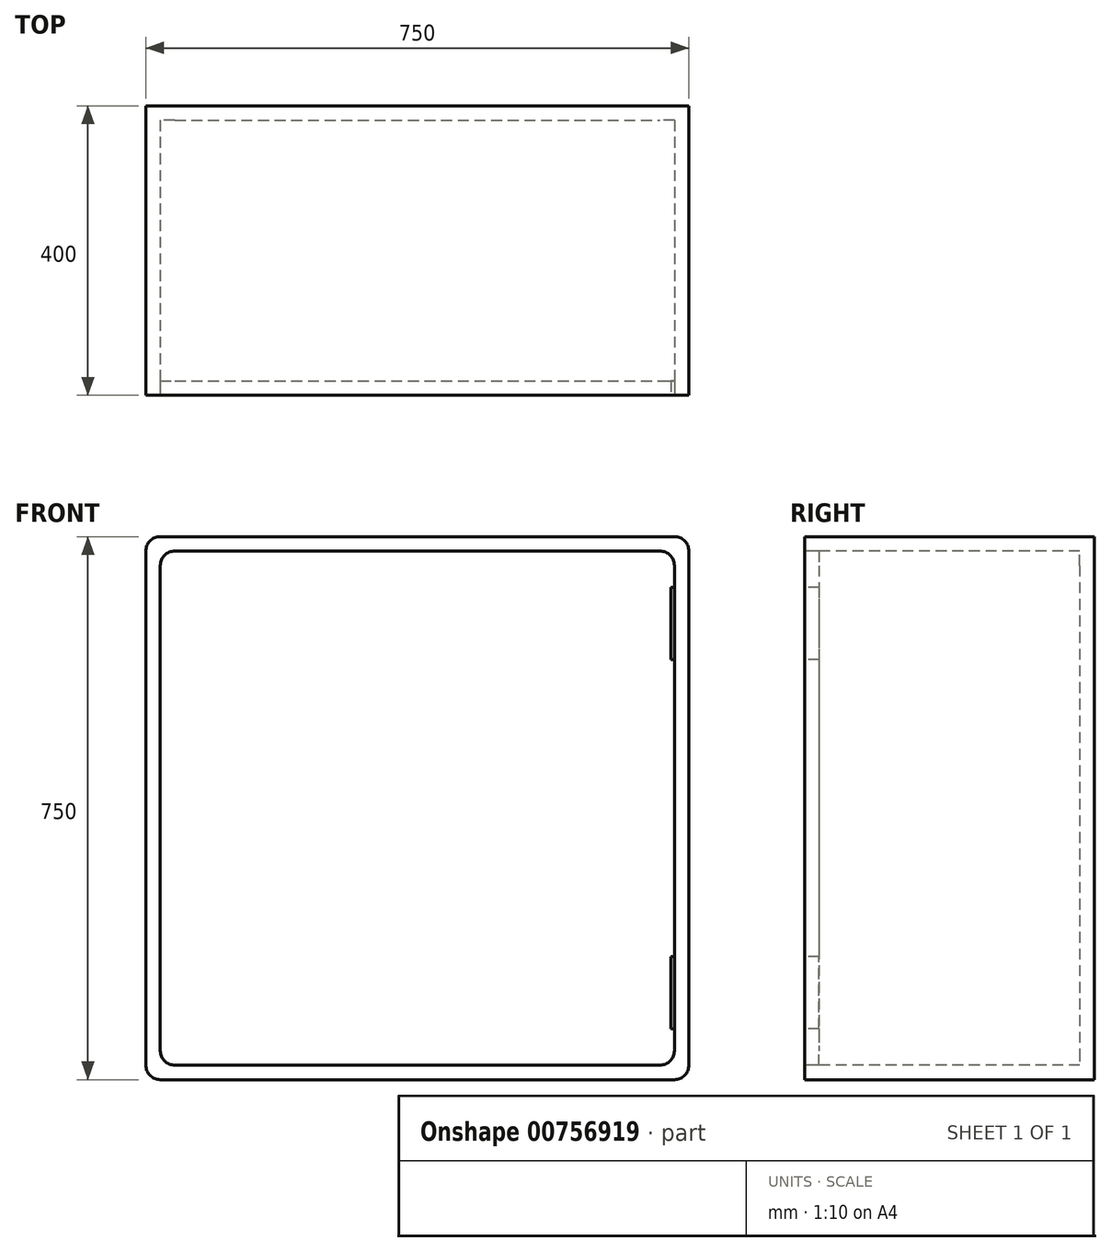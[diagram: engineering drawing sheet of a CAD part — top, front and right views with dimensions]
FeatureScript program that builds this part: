
annotation { "Feature Type Name" : "Feature", "Feature Type Description" : "" }
export const myFeature = defineFeature(function(context is Context, id is Id, definition is map)
    precondition{}
    {
        {
            var Q0;
            Q0=qCreatedBy(makeId("Front.planeOp"),FACE);
            var sketch = newSketch(context, id + "F0", { "sketchPlane" : qUnion([Q0])});
            skLineSegment(sketch, "E0.bottom", {"start": v(0, -20) * mm, "end": v(710, -20) * mm});
            skLineSegment(sketch, "E0.top", {"start": v(0, 730) * mm, "end": v(710, 730) * mm});
            skLineSegment(sketch, "E0.left", {"start": v(-20, 0) * mm, "end": v(-20, 710) * mm});
            skLineSegment(sketch, "E0.right", {"start": v(730, 0) * mm, "end": v(730, 710) * mm});
            skLineSegment(sketch, "E1.bottom", {"start": v(20, 710) * mm, "end": v(690, 710) * mm});
            skLineSegment(sketch, "E1.top", {"start": v(20, 0) * mm, "end": v(690, 0) * mm});
            skLineSegment(sketch, "E1.left", {"start": v(0, 690) * mm, "end": v(0, 20) * mm});
            skLineSegment(sketch, "E1.right", {"start": v(710, 690) * mm, "end": v(710, 20) * mm});
            skPoint(sketch, "E2.visualSharp", {"position": v(0, 710) * mm});
            skArc(sketch, "E2.filletArc", {"start": v(20, 710) * mm, "mid": v(5.86, 704.14) * mm, "end": v(0, 690) * mm});
            skPoint(sketch, "E3.visualSharp", {"position": v(-20, 730) * mm});
            skArc(sketch, "E3.filletArc", {"start": v(0, 730) * mm, "mid": v(-14.14, 724.14) * mm, "end": v(-20, 710) * mm});
            skArc(sketch, "E4.filletArc", {"start": v(730, 710) * mm, "mid": v(724.14, 724.14) * mm, "end": v(710, 730) * mm});
            skArc(sketch, "E5.filletArc", {"start": v(710, 690) * mm, "mid": v(704.14, 704.14) * mm, "end": v(690, 710) * mm});
            skPoint(sketch, "E6.visualSharp", {"position": v(730, -20) * mm});
            skArc(sketch, "E6.filletArc", {"start": v(710, -20) * mm, "mid": v(724.14, -14.14) * mm, "end": v(730, 0) * mm});
            skArc(sketch, "E7.filletArc", {"start": v(690, 0) * mm, "mid": v(704.14, 5.86) * mm, "end": v(710, 20) * mm});
            skPoint(sketch, "E8.visualSharp", {"position": v(-20, -20) * mm});
            skArc(sketch, "E8.filletArc", {"start": v(-20, 0) * mm, "mid": v(-14.14, -14.14) * mm, "end": v(0, -20) * mm});
            skArc(sketch, "E9.filletArc", {"start": v(0, 20) * mm, "mid": v(5.86, 5.86) * mm, "end": v(20, 0) * mm});
            skSolve(sketch);
        }
        {
            var Q0;
            Q0=makeQuery(id+"F0.imprint","IMPRINT",FACE,{"disambiguationData":[TD([[makeQuery(id+"F0.imprint","IMPRINT",EDGE,{"derivedFrom":sQuery(id+"F0.wireOp",EDGE,"E0.bottom")}),1.0]])]});
            var Q1;
            Q1=makeQuery(id+"F0.imprint","IMPRINT",FACE,{"disambiguationData":[TD([[makeQuery(id+"F0.imprint","IMPRINT",EDGE,{"derivedFrom":sQuery(id+"F0.wireOp",EDGE,"E1.bottom")}),-1.0]])]});
            extrude(context, id + "F1", {"entities" : qUnion([Q0, Q1]), "oppositeDirection" : true, "depth" : 400 * mm, "offsetDistance" : 25.4 * mm});
        }
        {
            var Q0;
            Q0=makeQuery(id+"F0.imprint","IMPRINT",FACE,{"disambiguationData":[TD([[makeQuery(id+"F0.imprint","IMPRINT",EDGE,{"derivedFrom":sQuery(id+"F0.wireOp",EDGE,"E1.bottom")}),-1.0]])]});
            extrude(context, id + "F2", {"entities" : qUnion([Q0]), "operationType" : NewBodyOperationType.REMOVE, "oppositeDirection" : true, "depth" : 380 * mm, "offsetDistance" : 25.4 * mm});
        }
        {
            var Q0;
            Q0=makeQuery(id+"F0.imprint","IMPRINT",FACE,{"disambiguationData":[TD([[makeQuery(id+"F0.imprint","IMPRINT",EDGE,{"derivedFrom":sQuery(id+"F0.wireOp",EDGE,"E1.bottom")}),-1.0]])]});
            extrude(context, id + "F3", {"entities" : qUnion([Q0]), "oppositeDirection" : true, "depth" : 20 * mm, "offsetDistance" : 25.4 * mm});
        }
        {
            var Q0;
            Q0=makeQuery(id+"F3.opExtrude","CAP_FACE",FACE,{"disambiguationData":[OSD([sQuery(id+"F0.wireOp",EDGE,"E1.bottom"),sQuery(id+"F0.wireOp",EDGE,"E1.top"),sQuery(id+"F0.wireOp",EDGE,"E1.left"),sQuery(id+"F0.wireOp",EDGE,"E1.right"),sQuery(id+"F0.wireOp",EDGE,"E2.filletArc"),sQuery(id+"F0.wireOp",EDGE,"E5.filletArc"),sQuery(id+"F0.wireOp",EDGE,"E7.filletArc"),sQuery(id+"F0.wireOp",EDGE,"E9.filletArc")])],"isStart":true});
            var sketch = newSketch(context, id + "F4", { "sketchPlane" : qUnion([Q0])});
            skLineSegment(sketch, "E10", {"start": v(710, 660) * mm, "end": v(705, 660) * mm});
            skLineSegment(sketch, "E11", {"start": v(705, 660) * mm, "end": v(705, 560) * mm});
            skLineSegment(sketch, "E12", {"start": v(705, 560) * mm, "end": v(710, 560) * mm});
            skLineSegment(sketch, "E13", {"start": v(710, 50) * mm, "end": v(705, 50) * mm});
            skLineSegment(sketch, "E14", {"start": v(705, 50) * mm, "end": v(705, 150) * mm});
            skLineSegment(sketch, "E15", {"start": v(705, 150) * mm, "end": v(710, 150) * mm});
            skLineSegment(sketch, "E16", {"start": v(710, 150) * mm, "end": v(710, 50) * mm});
            skSolve(sketch);
        }
        {
            var Q0;
            {var subQ0=sQuery(id+"F4.wireOp",EDGE,"E10");Q0=makeQuery(id+"F4.imprint","IMPRINT",FACE,{"disambiguationData":[TD([[makeQuery(id+"F4.imprint","IMPRINT",EDGE,{"derivedFrom":subQ0}),1.0]])]});}
            var Q1;
            Q1=makeQuery(id+"F4.imprint","IMPRINT",FACE,{"disambiguationData":[TD([[makeQuery(id+"F4.imprint","IMPRINT",EDGE,{"derivedFrom":sQuery(id+"F4.wireOp",EDGE,"E13")}),-1.0]])]});
            extrude(context, id + "F5", {"entities" : qUnion([Q0, Q1]), "operationType" : NewBodyOperationType.REMOVE, "oppositeDirection" : true, "depth" : 27.94 * mm, "offsetDistance" : 25.4 * mm});
        }
    });
